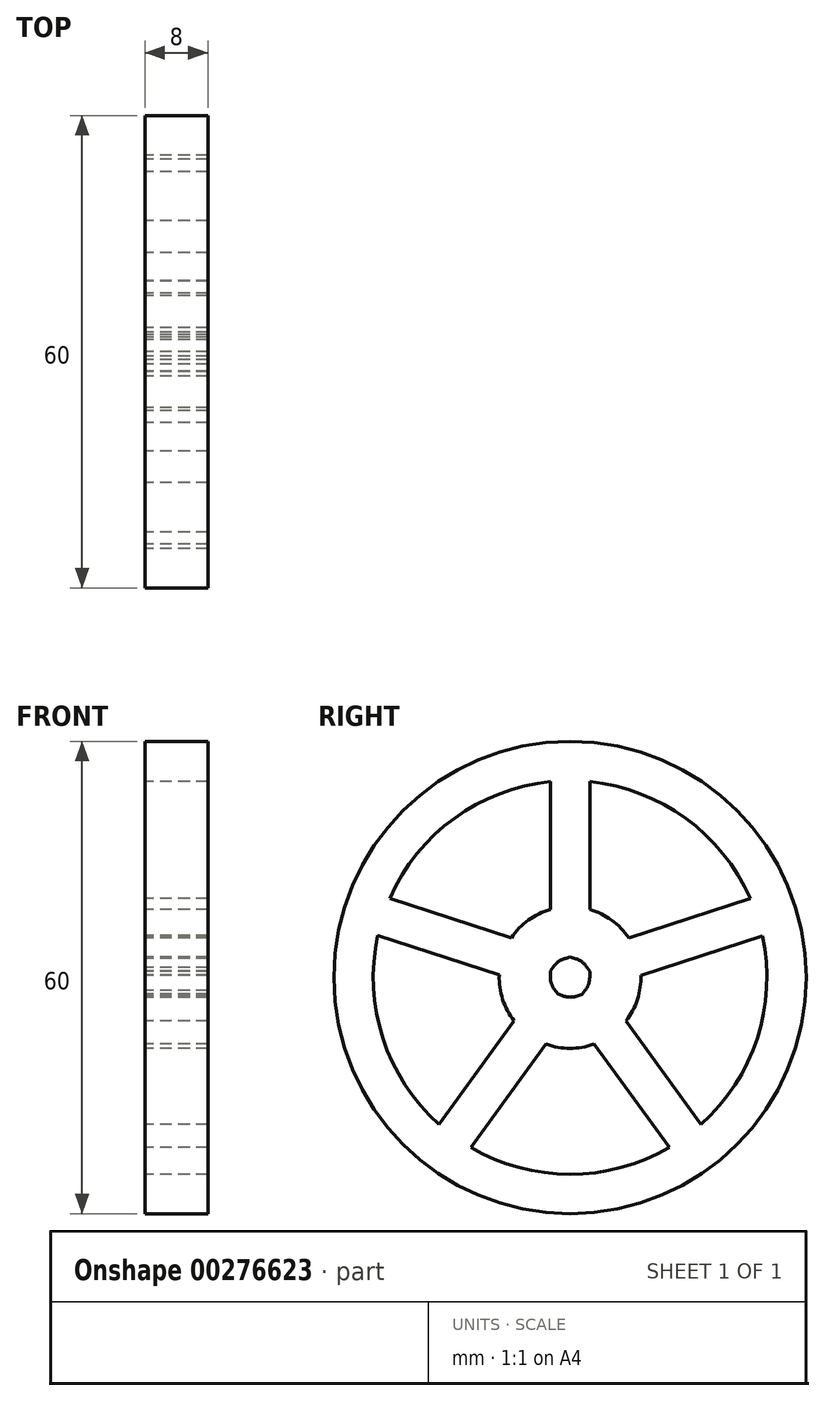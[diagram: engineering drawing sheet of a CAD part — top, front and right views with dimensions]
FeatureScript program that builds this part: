
annotation { "Feature Type Name" : "Feature", "Feature Type Description" : "" }
export const myFeature = defineFeature(function(context is Context, id is Id, definition is map)
    precondition{}
    {
        {
            var Q0;
            Q0=qCreatedBy(makeId("Right.planeOp"),FACE);
            var sketch = newSketch(context, id + "F0", { "sketchPlane" : qUnion([Q0])});
            skCircle(sketch, "E0", {"center": v(0, 0) * mm, "radius": 30 * mm});
            skArc(sketch, "E1", {"start": v(7.46, 5.04) * mm, "mid": v(5.3, 7.28) * mm, "end": v(2.5, 8.65) * mm});
            skArc(sketch, "E2", {"start": v(-2.49, 24.88) * mm, "mid": v(-14.69, 20.23) * mm, "end": v(-22.88, 10.06) * mm});
            skLineSegment(sketch, "E3.0", {"start": v(2.5, 0) * mm, "end": v(2.5, 0.8) * mm});
            skLineSegment(sketch, "E4.0", {"start": v(-2.49, 0) * mm, "end": v(-2.49, 0.83) * mm});
            skLineSegment(sketch, "E5.1.0", {"start": v(-0.77, -2.37) * mm, "end": v(-1.56, -2.1) * mm});
            skLineSegment(sketch, "E5.1.1", {"start": v(0.77, 2.38) * mm, "end": v(0.02, 2.62) * mm});
            skLineSegment(sketch, "E5.2.0", {"start": v(2.01, -1.46) * mm, "end": v(1.53, -2.13) * mm});
            skLineSegment(sketch, "E5.2.1", {"start": v(-2.02, 1.47) * mm, "end": v(-2.49, 0.83) * mm});
            skLineSegment(sketch, "E5.3.0", {"start": v(2.01, 1.46) * mm, "end": v(2.5, 0.8) * mm});
            skLineSegment(sketch, "E5.3.1", {"start": v(-2.02, -1.47) * mm, "end": v(-1.56, -2.1) * mm});
            skLineSegment(sketch, "E5.4.0", {"start": v(-0.77, 2.37) * mm, "end": v(0.02, 2.62) * mm});
            skLineSegment(sketch, "E5.4.1", {"start": v(0.77, -2.38) * mm, "end": v(1.53, -2.13) * mm});
            skArc(sketch, "E6.trimOffspring", {"start": v(-24.43, 5.32) * mm, "mid": v(-23.78, -7.72) * mm, "end": v(-16.64, -18.65) * mm});
            skArc(sketch, "E7.trimOffspring", {"start": v(-12.6, -21.59) * mm, "mid": v(0, -25) * mm, "end": v(12.6, -21.6) * mm});
            skArc(sketch, "E8.trimOffspring", {"start": v(16.63, -18.66) * mm, "mid": v(23.77, -7.73) * mm, "end": v(24.43, 5.3) * mm});
            skArc(sketch, "E9.trimOffspring", {"start": v(22.89, 10.05) * mm, "mid": v(14.7, 20.22) * mm, "end": v(2.5, 24.87) * mm});
            skArc(sketch, "E10.trimOffspring", {"start": v(-2.49, 8.65) * mm, "mid": v(-5.28, 7.28) * mm, "end": v(-7.45, 5.05) * mm});
            skArc(sketch, "E11.trimOffspring", {"start": v(-9, 0.3) * mm, "mid": v(-8.56, -2.78) * mm, "end": v(-7.1, -5.53) * mm});
            skArc(sketch, "E12.trimOffspring", {"start": v(-3.07, -8.46) * mm, "mid": v(0, -9) * mm, "end": v(3.06, -8.46) * mm});
            skArc(sketch, "E13.trimOffspring", {"start": v(7.1, -5.54) * mm, "mid": v(8.56, -2.79) * mm, "end": v(9, 0.3) * mm});
            skLineSegment(sketch, "E14.trimOffspring", {"start": v(7.1, -5.54) * mm, "end": v(16.7, -18.76) * mm});
            skLineSegment(sketch, "E15.trimOffspring", {"start": v(9, 0.3) * mm, "end": v(24.55, 5.35) * mm});
            skLineSegment(sketch, "E16.trimOffspring", {"start": v(7.46, 5.04) * mm, "end": v(23, 10.1) * mm});
            skLineSegment(sketch, "E17.trimOffspring", {"start": v(2.5, 8.65) * mm, "end": v(2.5, 25) * mm});
            skLineSegment(sketch, "E18.trimOffspring", {"start": v(-2.49, 8.65) * mm, "end": v(-2.49, 25) * mm});
            skLineSegment(sketch, "E19.trimOffspring", {"start": v(-7.45, 5.05) * mm, "end": v(-23, 10.1) * mm});
            skLineSegment(sketch, "E20.trimOffspring", {"start": v(-9, 0.3) * mm, "end": v(-24.55, 5.36) * mm});
            skLineSegment(sketch, "E21.trimOffspring", {"start": v(-7.1, -5.53) * mm, "end": v(-16.72, -18.76) * mm});
            skLineSegment(sketch, "E22.trimOffspring", {"start": v(-3.07, -8.46) * mm, "end": v(-12.68, -21.69) * mm});
            skLineSegment(sketch, "E23.trimOffspring", {"start": v(3.06, -8.46) * mm, "end": v(12.67, -21.7) * mm});
            skCircle(sketch, "E24", {"center": v(0, 0) * mm, "radius": 2.5 * mm});
            skSolve(sketch);
        }
        {
            var Q0;
            Q0=makeQuery(id+"F0.imprint","IMPRINT",FACE,{"disambiguationData":[TD([[makeQuery(id+"F0.imprint","IMPRINT",EDGE,{"derivedFrom":sQuery(id+"F0.wireOp",EDGE,"E0")}),1.0]])]});
            extrude(context, id + "F1", {"entities" : qUnion([Q0]), "depth" : 8 * mm});
        }
    });
